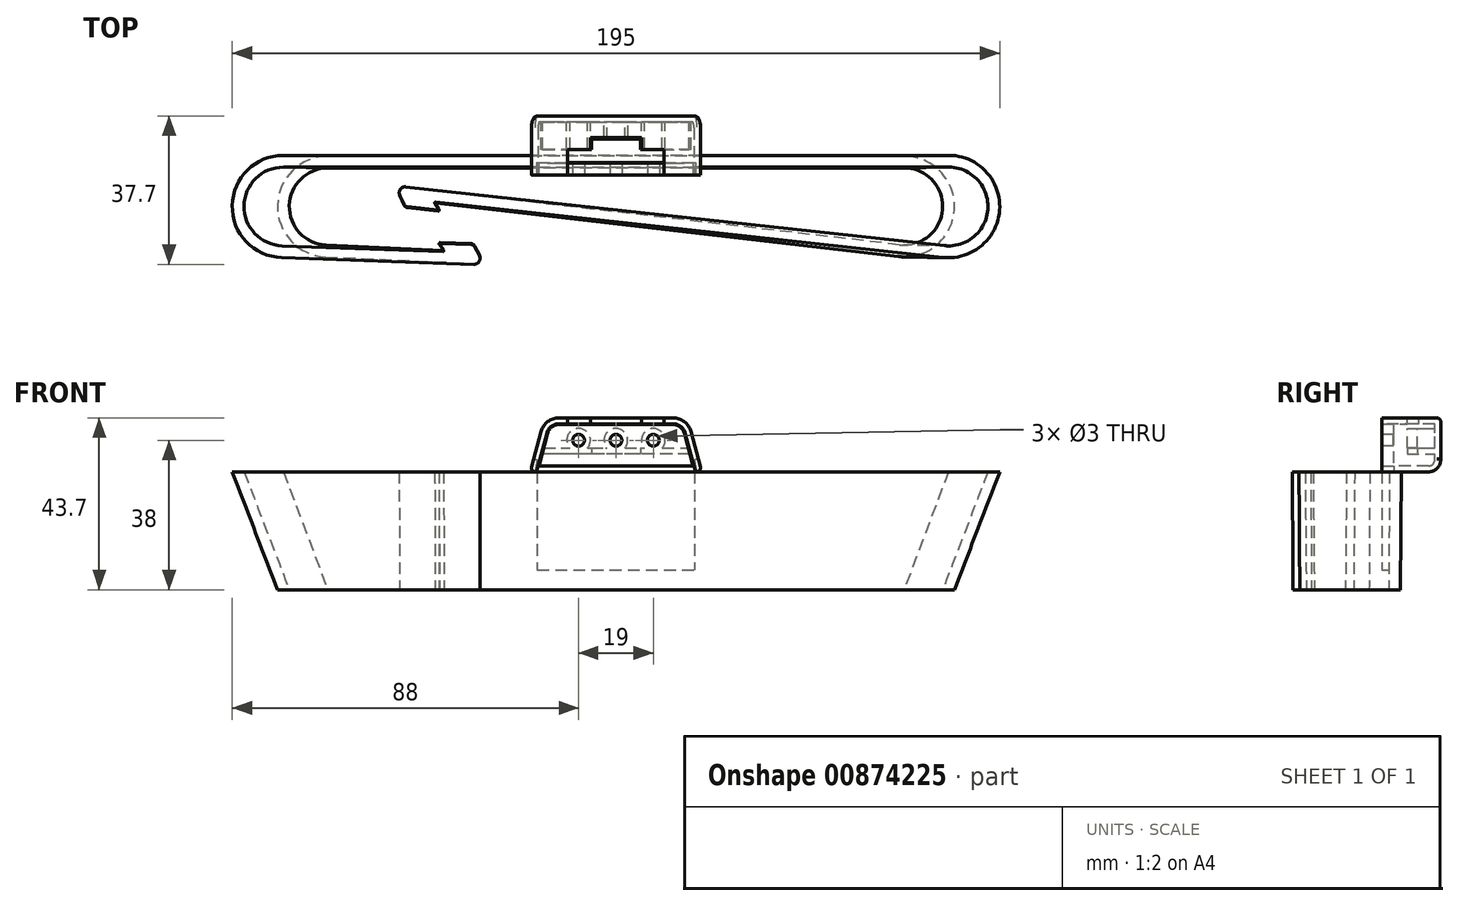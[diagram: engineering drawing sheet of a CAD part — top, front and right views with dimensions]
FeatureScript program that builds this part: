
annotation { "Feature Type Name" : "Feature", "Feature Type Description" : "" }
export const myFeature = defineFeature(function(context is Context, id is Id, definition is map)
    precondition{}
    {
        {
            var Q0;
            Q0=qCreatedBy(makeId("Top.planeOp"),FACE);
            var sketch = newSketch(context, id + "F0", { "sketchPlane" : qUnion([Q0])});
            skPoint(sketch, "E0.middle", {"position": v(0, 0) * mm});
            skArc(sketch, "E1", {"start": v(83.09, -12.92) * mm, "mid": v(97.48, -0.7) * mm, "end": v(84.5, 13) * mm});
            skLineSegment(sketch, "E2", {"start": v(84.5, 13) * mm, "end": v(-84.5, 13) * mm});
            skArc(sketch, "E3", {"start": v(-84.5, 13) * mm, "mid": v(-97.5, 0.23) * mm, "end": v(-84.95, -13) * mm});
            skLineSegment(sketch, "E4", {"start": v(83.09, -12.92) * mm, "end": v(-45.8, 1.15) * mm});
            skLineSegment(sketch, "E5", {"start": v(0, 13) * mm, "end": v(0, -3.85) * mm, "construction": true});
            skLineSegment(sketch, "E6", {"start": v(-33.5, 0) * mm, "end": v(-33.5, -14.79) * mm, "construction": true});
            skLineSegment(sketch, "E7", {"start": v(-84.95, -13) * mm, "end": v(-36.1, -14.7) * mm});
            skLineSegment(sketch, "E8", {"start": v(-84.5, 0) * mm, "end": v(-33.5, 0) * mm, "construction": true});
            skLineSegment(sketch, "E9.0", {"start": v(83.41, -9.94) * mm, "end": v(-53.4, 5) * mm});
            skLineSegment(sketch, "E9.1", {"start": v(-84.85, -10) * mm, "end": v(-43.96, -11.42) * mm});
            skArc(sketch, "E9.2", {"start": v(-84.5, 10) * mm, "mid": v(-94.5, 0.17) * mm, "end": v(-84.85, -10) * mm});
            skLineSegment(sketch, "E9.3", {"start": v(84.5, 10) * mm, "end": v(-84.5, 10) * mm});
            skArc(sketch, "E9.4", {"start": v(83.41, -9.94) * mm, "mid": v(94.49, -0.54) * mm, "end": v(84.5, 10) * mm});
            skLineSegment(sketch, "E10", {"start": v(-44.7, -9.4) * mm, "end": v(-36.79, -9.67) * mm});
            skLineSegment(sketch, "E11", {"start": v(-35.94, -10.2) * mm, "end": v(-34.72, -12.5) * mm});
            skPoint(sketch, "E12.visualSharp", {"position": v(-33.5, -14.79) * mm});
            skArc(sketch, "E12.filletArc", {"start": v(-36.1, -14.7) * mm, "mid": v(-34.77, -14) * mm, "end": v(-34.72, -12.5) * mm});
            skPoint(sketch, "E13.visualSharp", {"position": v(-36.21, -9.7) * mm});
            skArc(sketch, "E13.filletArc", {"start": v(-35.94, -10.2) * mm, "mid": v(-36.3, -9.82) * mm, "end": v(-36.79, -9.67) * mm});
            skPoint(sketch, "E14.visualSharp", {"position": v(-44.7, -9.4) * mm});
            skArc(sketch, "E14.filletArc", {"start": v(-44.7, -9.4) * mm, "mid": v(-44.9, -9.5) * mm, "end": v(-44.87, -9.72) * mm});
            skLineSegment(sketch, "E15", {"start": v(0, 0) * mm, "end": v(84.5, 0) * mm, "construction": true});
            skLineSegment(sketch, "E16", {"start": v(-46, 0.84) * mm, "end": v(-45.02, -0.61) * mm});
            skLineSegment(sketch, "E17", {"start": v(-45.2, -0.92) * mm, "end": v(-53.08, -0.06) * mm});
            skLineSegment(sketch, "E18", {"start": v(-53.9, 0.53) * mm, "end": v(-54.94, 2.9) * mm});
            skPoint(sketch, "E19.visualSharp", {"position": v(-53.66, 0) * mm});
            skArc(sketch, "E19.filletArc", {"start": v(-53.9, 0.53) * mm, "mid": v(-53.57, 0.12) * mm, "end": v(-53.08, -0.06) * mm});
            skPoint(sketch, "E20.visualSharp", {"position": v(-55.98, 5.28) * mm});
            skArc(sketch, "E20.filletArc", {"start": v(-53.4, 5) * mm, "mid": v(-54.77, 4.4) * mm, "end": v(-54.94, 2.9) * mm});
            skArc(sketch, "E21.filletArc", {"start": v(-45.2, -0.92) * mm, "mid": v(-45.02, -0.83) * mm, "end": v(-45.02, -0.61) * mm});
            skPoint(sketch, "E22.visualSharp", {"position": v(-46.23, 1.2) * mm});
            skArc(sketch, "E22.filletArc", {"start": v(-45.8, 1.15) * mm, "mid": v(-46, 1.06) * mm, "end": v(-46, 0.84) * mm});
            skLineSegment(sketch, "E23", {"start": v(-33.5, 0) * mm, "end": v(0, 0) * mm, "construction": true});
            skArc(sketch, "E24", {"start": v(-43.96, -11.42) * mm, "mid": v(-43.77, -11.31) * mm, "end": v(-43.8, -11.1) * mm});
            skLineSegment(sketch, "E25", {"start": v(-44.87, -9.72) * mm, "end": v(-43.8, -11.1) * mm});
            skLineSegment(sketch, "E26", {"start": v(-44.87, -9.47) * mm, "end": v(-44.87, -10.97) * mm, "construction": true});
            skLineSegment(sketch, "E27", {"start": v(-45.02, -0.61) * mm, "end": v(-45.02, 0.89) * mm, "construction": true});
            skSolve(sketch);
        }
        {
            var Q0;
            Q0=qCreatedBy(makeId("Top.planeOp"),FACE);
            cPlane(context, id + "F1", {"entities" : qUnion([Q0]), "cplaneType" : CPlaneType.OFFSET, "offset" : 30 * mm, "oppositeDirection" : true, "width" : 150 * mm, "height" : 150 * mm});
        }
        {
            var Q0;
            Q0=qCreatedBy(id+"F1.planeOp",FACE);
            var sketch = newSketch(context, id + "F2", { "sketchPlane" : qUnion([Q0])});
            skPoint(sketch, "E28.middle", {"position": v(0, 0) * mm});
            skArc(sketch, "E29", {"start": v(71.73, -12.71) * mm, "mid": v(85.98, -0.74) * mm, "end": v(73.2, 12.8) * mm});
            skLineSegment(sketch, "E30", {"start": v(73.2, 12.8) * mm, "end": v(-73.2, 12.8) * mm});
            skArc(sketch, "E31", {"start": v(-73.2, 12.8) * mm, "mid": v(-86, 0.3) * mm, "end": v(-73.78, -12.79) * mm});
            skLineSegment(sketch, "E32", {"start": v(71.73, -12.71) * mm, "end": v(-45.74, 0.9) * mm});
            skLineSegment(sketch, "E33", {"start": v(0, 12.8) * mm, "end": v(0, -4.4) * mm, "construction": true});
            skLineSegment(sketch, "E34", {"start": v(-33.5, 0) * mm, "end": v(-33.5, -14.62) * mm, "construction": true});
            skLineSegment(sketch, "E35", {"start": v(-73.78, -12.79) * mm, "end": v(-36.1, -14.5) * mm});
            skLineSegment(sketch, "E36", {"start": v(-73.2, 0) * mm, "end": v(-33.5, 0) * mm, "construction": true});
            skLineSegment(sketch, "E37.0", {"start": v(72.07, -9.73) * mm, "end": v(-53.31, 4.8) * mm});
            skLineSegment(sketch, "E37.1", {"start": v(-73.64, -9.79) * mm, "end": v(-43.92, -11.14) * mm});
            skArc(sketch, "E37.2", {"start": v(-73.2, 9.8) * mm, "mid": v(-83, 0.22) * mm, "end": v(-73.64, -9.79) * mm});
            skLineSegment(sketch, "E37.3", {"start": v(73.2, 9.8) * mm, "end": v(-73.2, 9.8) * mm});
            skArc(sketch, "E37.4", {"start": v(72.07, -9.73) * mm, "mid": v(82.98, -0.57) * mm, "end": v(73.2, 9.8) * mm});
            skLineSegment(sketch, "E38", {"start": v(-44.65, -9.1) * mm, "end": v(-36.73, -9.46) * mm});
            skLineSegment(sketch, "E39", {"start": v(-35.9, -10) * mm, "end": v(-34.7, -12.3) * mm});
            skPoint(sketch, "E40.visualSharp", {"position": v(-33.5, -14.62) * mm});
            skArc(sketch, "E40.filletArc", {"start": v(-36.1, -14.5) * mm, "mid": v(-34.76, -13.8) * mm, "end": v(-34.7, -12.3) * mm});
            skPoint(sketch, "E41.visualSharp", {"position": v(-36.16, -9.5) * mm});
            skArc(sketch, "E41.filletArc", {"start": v(-35.9, -10) * mm, "mid": v(-36.24, -9.62) * mm, "end": v(-36.73, -9.46) * mm});
            skPoint(sketch, "E42.visualSharp", {"position": v(-44.65, -9.1) * mm});
            skArc(sketch, "E42.filletArc", {"start": v(-44.65, -9.1) * mm, "mid": v(-44.83, -9.21) * mm, "end": v(-44.82, -9.43) * mm});
            skLineSegment(sketch, "E43", {"start": v(0, 0) * mm, "end": v(73.2, 0) * mm, "construction": true});
            skLineSegment(sketch, "E44", {"start": v(-45.93, 0.6) * mm, "end": v(-44.97, -0.87) * mm});
            skLineSegment(sketch, "E45", {"start": v(-45.16, -1.18) * mm, "end": v(-53.03, -0.27) * mm});
            skLineSegment(sketch, "E46", {"start": v(-53.83, 0.33) * mm, "end": v(-54.86, 2.71) * mm});
            skPoint(sketch, "E47.visualSharp", {"position": v(-53.6, -0.2) * mm});
            skArc(sketch, "E47.filletArc", {"start": v(-53.83, 0.33) * mm, "mid": v(-53.5, -0.08) * mm, "end": v(-53.03, -0.27) * mm});
            skPoint(sketch, "E48.visualSharp", {"position": v(-55.9, 5.1) * mm});
            skArc(sketch, "E48.filletArc", {"start": v(-53.31, 4.8) * mm, "mid": v(-54.69, 4.2) * mm, "end": v(-54.86, 2.71) * mm});
            skArc(sketch, "E49.filletArc", {"start": v(-45.16, -1.18) * mm, "mid": v(-44.96, -1.08) * mm, "end": v(-44.97, -0.87) * mm});
            skPoint(sketch, "E50.visualSharp", {"position": v(-46.17, 0.95) * mm});
            skArc(sketch, "E50.filletArc", {"start": v(-45.74, 0.9) * mm, "mid": v(-45.93, 0.8) * mm, "end": v(-45.93, 0.6) * mm});
            skLineSegment(sketch, "E51", {"start": v(-33.5, 0) * mm, "end": v(0, 0) * mm, "construction": true});
            skArc(sketch, "E52", {"start": v(-43.92, -11.14) * mm, "mid": v(-43.73, -11.03) * mm, "end": v(-43.75, -10.82) * mm});
            skLineSegment(sketch, "E53", {"start": v(-44.82, -9.43) * mm, "end": v(-43.75, -10.82) * mm});
            skLineSegment(sketch, "E54", {"start": v(-44.82, -9.18) * mm, "end": v(-44.82, -10.68) * mm, "construction": true});
            skLineSegment(sketch, "E55", {"start": v(-44.97, -0.87) * mm, "end": v(-44.97, 0.63) * mm, "construction": true});
            skSolve(sketch);
        }
        {
            var Q0;
            Q0=qSketchRegion(id+"F0",true);
            var Q1;
            Q1=qSketchRegion(id+"F2",true);
            loft(context, id + "F3", {"sheetProfilesArray" : [{ "sheetProfileEntities" : qUnion([Q0]) }, { "sheetProfileEntities" : qUnion([Q1]) }]});
        }
        {
            var Q0;
            Q0=qCreatedBy(makeId("Top.planeOp"),FACE);
            var sketch = newSketch(context, id + "F4", { "sketchPlane" : qUnion([Q0])});
            skLineSegment(sketch, "E56", {"start": v(20, 11) * mm, "end": v(20, 8) * mm});
            skLineSegment(sketch, "E57", {"start": v(-20, 8) * mm, "end": v(-20, 11) * mm});
            skLineSegment(sketch, "E58", {"start": v(0, 8) * mm, "end": v(0, 10) * mm, "construction": true});
            skPoint(sketch, "E58.endSnap0", {"position": v(0, 10) * mm});
            skLineSegment(sketch, "E59", {"start": v(-20, 8) * mm, "end": v(20, 8) * mm});
            skLineSegment(sketch, "E60", {"start": v(-20, 11) * mm, "end": v(20, 11) * mm});
            skSolve(sketch);
        }
        {
            var Q0;
            Q0=qSketchRegion(id+"F4",true);
            extrude(context, id + "F5", {"entities" : qUnion([Q0]), "operationType" : NewBodyOperationType.ADD, "depth" : 12 * mm, "offsetDistance" : 25 * mm, "hasSecondDirection" : true, "secondDirectionOppositeDirection" : true, "secondDirectionDepth" : 25 * mm});
        }
        {
            var Q0;
            Q0=makeQuery(id+"F5.opExtrude","SWEPT_FACE",FACE,{"disambiguationData":[OSD([sQuery(id+"F4.wireOp",EDGE,"E59")])]});
            var sketch = newSketch(context, id + "F6", { "sketchPlane" : qUnion([Q0])});
            skLineSegment(sketch, "E61", {"start": v(0, 12) * mm, "end": v(0, 8) * mm, "construction": true});
            skCircle(sketch, "E62", {"center": v(0, 8) * mm, "radius": 1.5 * mm});
            skCircle(sketch, "E63", {"center": v(9.5, 8) * mm, "radius": 1.5 * mm});
            skCircle(sketch, "E64", {"center": v(-9.5, 8) * mm, "radius": 1.5 * mm});
            skSolve(sketch);
        }
        {
            var Q0;
            Q0=qSketchRegion(id+"F6",true);
            extrude(context, id + "F7", {"entities" : qUnion([Q0]), "operationType" : NewBodyOperationType.REMOVE, "endBound" : BoundingType.THROUGH_ALL, "oppositeDirection" : true, "depth" : 25 * mm, "offsetDistance" : 25 * mm});
        }
        {
            var Q0;
            Q0=makeQuery(id+"F5.opExtrude","CAP_EDGE",EDGE,{"disambiguationData":[OSD([sQuery(id+"F4.wireOp",EDGE,"E57")])],"isStart":false});
            var Q1;
            Q1=makeQuery(id+"F5.opExtrude","CAP_EDGE",EDGE,{"disambiguationData":[OSD([sQuery(id+"F4.wireOp",EDGE,"E56")])],"isStart":false});
            chamfer(context, id + "F8", {"entities" : qUnion([Q0, Q1]), "chamferType" : ChamferType.OFFSET_ANGLE, "width" : 12 * mm, "oppositeDirection" : false, "angle" : 15 * degree, "tangentPropagation" : true});
        }
        {
            var Q0;
            {var subQ0=sQuery(id+"F4.wireOp",EDGE,"E57");Q0=makeQuery(id+"F8.opChamfer","BLEND_EDGE",EDGE,{"blendedFrom":[makeQuery(id+"F5.opExtrude","CAP_EDGE",EDGE,{"disambiguationData":[OSD([subQ0])],"isStart":false}),makeQuery(id+"F5.opExtrude","CAP_FACE",FACE,{"disambiguationData":[OSD([sQuery(id+"F4.wireOp",EDGE,"E56"),sQuery(id+"F4.wireOp",EDGE,"wCvbTNE0-mzVd-2HxN-2LCz-JJ2DgGp3YGLQ"),subQ0,sQuery(id+"F4.wireOp",EDGE,"oFSy1M9t-5aWS-44CZ-ftMe-uW2eaNrki7Xb")])],"isStart":false})],"blendedInto":[makeQuery(id+"F5.opExtrude","CAP_FACE",FACE,{"disambiguationData":[OSD([sQuery(id+"F4.wireOp",EDGE,"E56"),sQuery(id+"F4.wireOp",EDGE,"wCvbTNE0-mzVd-2HxN-2LCz-JJ2DgGp3YGLQ"),subQ0,sQuery(id+"F4.wireOp",EDGE,"oFSy1M9t-5aWS-44CZ-ftMe-uW2eaNrki7Xb")])],"isStart":false})]});}
            var Q1;
            {var subQ0=sQuery(id+"F4.wireOp",EDGE,"E56");Q1=makeQuery(id+"F8.opChamfer","BLEND_EDGE",EDGE,{"blendedFrom":[makeQuery(id+"F5.opExtrude","CAP_EDGE",EDGE,{"disambiguationData":[OSD([subQ0])],"isStart":false}),makeQuery(id+"F5.opExtrude","CAP_FACE",FACE,{"disambiguationData":[OSD([subQ0,sQuery(id+"F4.wireOp",EDGE,"wCvbTNE0-mzVd-2HxN-2LCz-JJ2DgGp3YGLQ"),sQuery(id+"F4.wireOp",EDGE,"E57"),sQuery(id+"F4.wireOp",EDGE,"oFSy1M9t-5aWS-44CZ-ftMe-uW2eaNrki7Xb")])],"isStart":false})],"blendedInto":[makeQuery(id+"F5.opExtrude","CAP_FACE",FACE,{"disambiguationData":[OSD([subQ0,sQuery(id+"F4.wireOp",EDGE,"wCvbTNE0-mzVd-2HxN-2LCz-JJ2DgGp3YGLQ"),sQuery(id+"F4.wireOp",EDGE,"E57"),sQuery(id+"F4.wireOp",EDGE,"oFSy1M9t-5aWS-44CZ-ftMe-uW2eaNrki7Xb")])],"isStart":false})]});}
            fillet(context, id + "F9", {"entities" : qUnion([Q0, Q1]), "radius" : 3 * mm, "tangentPropagation" : true, "allowEdgeOverflow" : false});
        }
        {
            var Q0;
            Q0=makeQuery(id+"F5.opExtrude","SWEPT_FACE",FACE,{"disambiguationData":[OSD([sQuery(id+"F4.wireOp",EDGE,"E59")])]});
            cPlane(context, id + "F10", {"entities" : qUnion([Q0]), "cplaneType" : CPlaneType.OFFSET, "offset" : 0 * mm, "oppositeDirection" : true, "width" : 150 * mm, "height" : 150 * mm});
        }
        {
            var Q0;
            Q0=qCreatedBy(id+"F10.planeOp",FACE);
            var sketch = newSketch(context, id + "F11", { "sketchPlane" : qUnion([Q0])});
            skLineSegment(sketch, "E65.0", {"start": v(-19.02, 10.22) * mm, "end": v(-21.76, 0) * mm});
            skLineSegment(sketch, "E65.1", {"start": v(21.76, 0) * mm, "end": v(19.02, 10.22) * mm});
            skArc(sketch, "E65.2", {"start": v(19.02, 10.22) * mm, "mid": v(17.34, 12.73) * mm, "end": v(14.48, 13.7) * mm});
            skLineSegment(sketch, "E65.3", {"start": v(-14.48, 13.7) * mm, "end": v(14.48, 13.7) * mm});
            skArc(sketch, "E65.4", {"start": v(-14.48, 13.7) * mm, "mid": v(-17.34, 12.73) * mm, "end": v(-19.02, 10.22) * mm});
            skLineSegment(sketch, "E66", {"start": v(-21.76, 0) * mm, "end": v(21.76, 0) * mm});
            skSolve(sketch);
        }
        {
            var Q0;
            Q0=qSketchRegion(id+"F11",true);
            extrude(context, id + "F12", {"entities" : qUnion([Q0]), "oppositeDirection" : true, "depth" : 15 * mm, "offsetDistance" : 25 * mm});
        }
        {
            var Q0;
            Q0=makeQuery(id+"F12.opExtrude","CAP_EDGE",EDGE,{"disambiguationData":[OSD([sQuery(id+"F11.wireOp",EDGE,"E66")])],"isStart":false});
            fillet(context, id + "F13", {"entities" : qUnion([Q0]), "radius" : 3 * mm, "tangentPropagation" : true, "allowEdgeOverflow" : false});
        }
        {
            var Q0;
            Q0=makeQuery(id+"F12.opExtrude","CAP_FACE",FACE,{"disambiguationData":[OSD([sQuery(id+"F11.wireOp",EDGE,"E65.0"),sQuery(id+"F11.wireOp",EDGE,"E65.1"),sQuery(id+"F11.wireOp",EDGE,"E65.2"),sQuery(id+"F11.wireOp",EDGE,"E65.3"),sQuery(id+"F11.wireOp",EDGE,"E65.4"),sQuery(id+"F11.wireOp",EDGE,"E66")])],"isStart":true});
            shell(context, id + "F14", {"entities" : qUnion([Q0]), "thickness" : 1.5 * mm});
        }
        {
            var Q0;
            Q0=makeQuery(id+"F12.opExtrude","CAP_FACE",FACE,{"disambiguationData":[OSD([sQuery(id+"F11.wireOp",EDGE,"E65.0"),sQuery(id+"F11.wireOp",EDGE,"E65.1"),sQuery(id+"F11.wireOp",EDGE,"E65.2"),sQuery(id+"F11.wireOp",EDGE,"E65.3"),sQuery(id+"F11.wireOp",EDGE,"E65.4"),sQuery(id+"F11.wireOp",EDGE,"E66")])],"isStart":true});
            var sketch = newSketch(context, id + "F15", { "sketchPlane" : qUnion([Q0])});
            skLineSegment(sketch, "E67", {"start": v(-19.8, 1.5) * mm, "end": v(19.8, 1.5) * mm});
            skLineSegment(sketch, "E68", {"start": v(19.8, 1.5) * mm, "end": v(20.2, 0) * mm});
            skLineSegment(sketch, "E69", {"start": v(20.2, 0) * mm, "end": v(-20.2, 0) * mm});
            skLineSegment(sketch, "E70", {"start": v(-20.2, 0) * mm, "end": v(-19.8, 1.5) * mm});
            skPoint(sketch, "E71", {"position": v(0, 0) * mm});
            skSolve(sketch);
        }
        {
            var Q0;
            Q0=qSketchRegion(id+"F15",true);
            extrude(context, id + "F16", {"entities" : qUnion([Q0]), "operationType" : NewBodyOperationType.REMOVE, "oppositeDirection" : true, "depth" : 3.1 * mm, "offsetDistance" : 25 * mm});
        }
        {
            var Q0;
            Q0=makeQuery(id+"F12.opExtrude","SWEPT_EDGE",EDGE,{"disambiguationData":[OSD([sQuery(id+"F11.wireOp",EDGE,"E65.1"),sQuery(id+"F11.wireOp",EDGE,"E66")])]});
            fillet(context, id + "F17", {"entities" : qUnion([Q0]), "radius" : 1 * mm, "tangentPropagation" : true, "allowEdgeOverflow" : false});
        }
        {
            var Q0;
            Q0=makeQuery(id+"F14.opShell","OFFSET_FACE",FACE,{"disambiguationData":[OSD([sQuery(id+"F11.wireOp",EDGE,"E65.0"),sQuery(id+"F11.wireOp",EDGE,"E65.1"),sQuery(id+"F11.wireOp",EDGE,"E65.2"),sQuery(id+"F11.wireOp",EDGE,"E65.3"),sQuery(id+"F11.wireOp",EDGE,"E65.4"),sQuery(id+"F11.wireOp",EDGE,"E66")])]});
            var sketch = newSketch(context, id + "F18", { "sketchPlane" : qUnion([Q0])});
            skCircle(sketch, "E72", {"center": v(0, 8) * mm, "radius": 3 * mm});
            skCircle(sketch, "E73", {"center": v(9.5, 8) * mm, "radius": 3 * mm});
            skCircle(sketch, "E74", {"center": v(-9.5, 8) * mm, "radius": 3 * mm});
            skLineSegment(sketch, "E75", {"start": v(-18.6, 6) * mm, "end": v(18.6, 6) * mm});
            skLineSegment(sketch, "E76", {"start": v(18.6, 6) * mm, "end": v(19, 4.5) * mm});
            skLineSegment(sketch, "E77", {"start": v(19, 4.5) * mm, "end": v(-19, 4.5) * mm});
            skLineSegment(sketch, "E78", {"start": v(-19, 4.5) * mm, "end": v(-18.6, 6) * mm});
            skSolve(sketch);
        }
        {
            var Q0;
            Q0=makeQuery(id+"F18.imprint","IMPRINT",FACE,{"disambiguationData":[TD([[makeQuery(id+"F18.imprint","IMPRINT",EDGE,{"derivedFrom":sQuery(id+"F18.wireOp",EDGE,"E74")}),1.0]])]});
            var Q1;
            Q1=makeQuery(id+"F18.imprint","IMPRINT",FACE,{"disambiguationData":[TD([[makeQuery(id+"F18.imprint","IMPRINT",EDGE,{"derivedFrom":sQuery(id+"F18.wireOp",EDGE,"E73")}),1.0]])]});
            var Q2;
            {var subQ0=sQuery(id+"F18.wireOp",EDGE,"E76");Q2=makeQuery(id+"F18.imprint","IMPRINT",FACE,{"disambiguationData":[TD([[makeQuery(id+"F18.imprint","IMPRINT",EDGE,{"derivedFrom":subQ0}),1.0]])]});}
            var Q3;
            {var subQ0=sQuery(id+"F18.wireOp",EDGE,"E75");var subQ1=sQuery(id+"F18.wireOp",EDGE,"E72");var subQ2=makeQuery(id+"F18.imprint","INTERSECT",VERTEX,{"disambiguationData":[OD(0.0)],"derivedFrom":[subQ1,subQ0]});Q3=makeQuery(id+"F18.imprint","IMPRINT",FACE,{"disambiguationData":[TD([[makeQuery(id+"F18.imprint","IMPRINT",EDGE,{"disambiguationData":[TD([[subQ2,1.0]])],"derivedFrom":subQ1}),1.0]])]});}
            var Q4;
            {var subQ0=sQuery(id+"F18.wireOp",EDGE,"E75");var subQ1=sQuery(id+"F18.wireOp",EDGE,"E72");var subQ2=makeQuery(id+"F18.imprint","INTERSECT",VERTEX,{"disambiguationData":[OD(0.0)],"derivedFrom":[subQ1,subQ0]});Q4=makeQuery(id+"F18.imprint","IMPRINT",FACE,{"disambiguationData":[TD([[makeQuery(id+"F18.imprint","IMPRINT",EDGE,{"disambiguationData":[TD([[subQ2,-1.0]])],"derivedFrom":subQ1}),1.0]])]});}
            extrude(context, id + "F19", {"entities" : qUnion([Q0, Q1, Q2, Q3, Q4]), "operationType" : NewBodyOperationType.ADD, "depth" : 7 * mm, "offsetDistance" : 25 * mm});
        }
        {
            var Q0;
            Q0=makeQuery(id+"F12.opExtrude","SWEPT_FACE",FACE,{"disambiguationData":[OSD([sQuery(id+"F11.wireOp",EDGE,"E65.3")])]});
            var sketch = newSketch(context, id + "F20", { "sketchPlane" : qUnion([Q0])});
            skLineSegment(sketch, "E79", {"start": v(-12.25, 8) * mm, "end": v(-12.25, 14.5) * mm});
            skLineSegment(sketch, "E80", {"start": v(-12.25, 14.5) * mm, "end": v(-6.5, 14.5) * mm});
            skLineSegment(sketch, "E81", {"start": v(-6.5, 14.5) * mm, "end": v(-6.5, 17.5) * mm});
            skLineSegment(sketch, "E82", {"start": v(-6.5, 17.5) * mm, "end": v(6.5, 17.5) * mm});
            skLineSegment(sketch, "E83", {"start": v(6.5, 17.5) * mm, "end": v(6.5, 14.5) * mm});
            skLineSegment(sketch, "E84", {"start": v(6.5, 14.5) * mm, "end": v(12.25, 14.5) * mm});
            skLineSegment(sketch, "E85", {"start": v(12.25, 14.5) * mm, "end": v(12.25, 8) * mm});
            skLineSegment(sketch, "E86", {"start": v(12.25, 8) * mm, "end": v(-12.25, 8) * mm});
            skPoint(sketch, "E87", {"position": v(0, 8) * mm});
            skSolve(sketch);
        }
        {
            var Q0;
            Q0=qSketchRegion(id+"F20",true);
            extrude(context, id + "F21", {"entities" : qUnion([Q0]), "operationType" : NewBodyOperationType.REMOVE, "oppositeDirection" : true, "depth" : 1.5 * mm, "offsetDistance" : 25 * mm});
        }
        {
            var Q0;
            {var subQ0=sQuery(id+"F11.wireOp",EDGE,"E66");Q0=makeQuery(id+"F14.opShell","OFFSET_FACE",FACE,{"disambiguationData":[OSD([subQ0]),TDD([makeQuery(id+"F12.opExtrude","SWEPT_FACE",FACE,{"disambiguationData":[OSD([subQ0])]})])]});}
            var sketch = newSketch(context, id + "F22", { "sketchPlane" : qUnion([Q0])});
            skLineSegment(sketch, "E88.bottom", {"start": v(6.25, 11.1) * mm, "end": v(-6.25, 11.1) * mm});
            skLineSegment(sketch, "E88.top", {"start": v(6.25, 17.1) * mm, "end": v(-6.25, 17.1) * mm});
            skLineSegment(sketch, "E88.left", {"start": v(6.25, 11.1) * mm, "end": v(6.25, 17.1) * mm});
            skLineSegment(sketch, "E88.right", {"start": v(-6.25, 11.1) * mm, "end": v(-6.25, 17.1) * mm});
            skPoint(sketch, "E89", {"position": v(0, 11.1) * mm});
            skSolve(sketch);
        }
        {
            var Q0;
            Q0=makeQuery(id+"F22.imprint","IMPRINT",FACE,{"disambiguationData":[TD([[makeQuery(id+"F22.imprint","IMPRINT",EDGE,{"derivedFrom":sQuery(id+"F22.wireOp",EDGE,"E88.bottom")}),1.0]])]});
            extrude(context, id + "F23", {"entities" : qUnion([Q0]), "operationType" : NewBodyOperationType.REMOVE, "depth" : 25 * mm, "offsetDistance" : 25 * mm});
        }
    });
